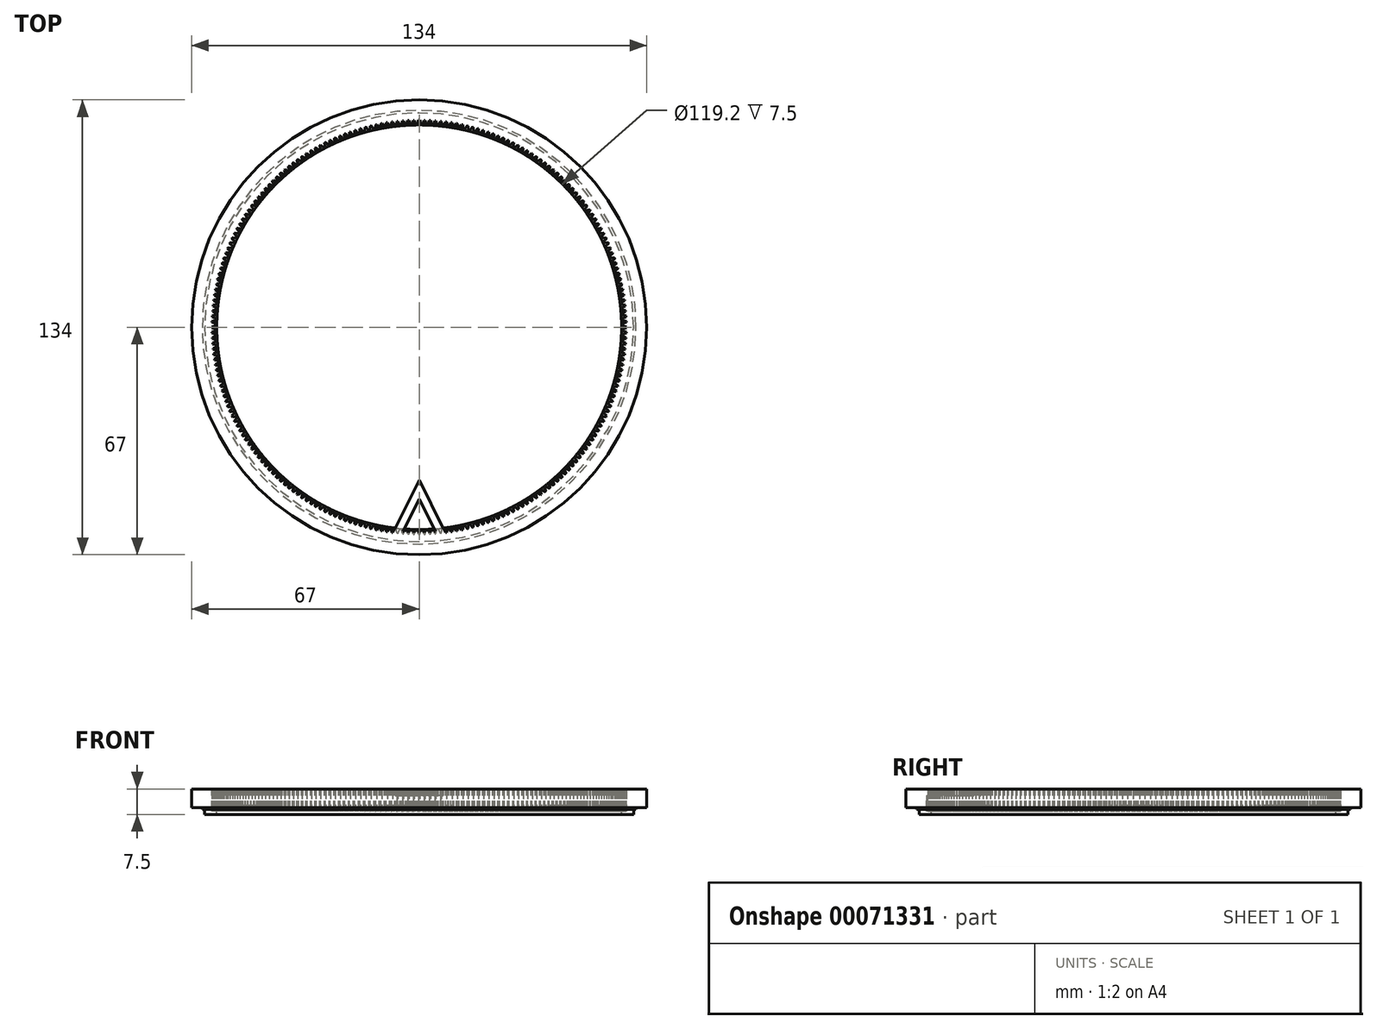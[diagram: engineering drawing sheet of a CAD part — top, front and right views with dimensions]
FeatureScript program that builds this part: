
annotation { "Feature Type Name" : "Feature", "Feature Type Description" : "" }
export const myFeature = defineFeature(function(context is Context, id is Id, definition is map)
    precondition{}
    {
        {
            var Q0;
            Q0=qCreatedBy(makeId("Front.planeOp"),FACE);
            var sketch = newSketch(context, id + "F0", { "sketchPlane" : qUnion([Q0])});
            skCircle(sketch, "E0", {"center": v(0, 0) * mm, "radius": 67 * mm});
            skCircle(sketch, "E1", {"center": v(0, 0) * mm, "radius": 59.6 * mm});
            skSolve(sketch);
        }
        {
            var Q0;
            Q0=makeQuery(id+"F0.imprint","IMPRINT",FACE,{"disambiguationData":[TD([[makeQuery(id+"F0.imprint","IMPRINT",EDGE,{"derivedFrom":sQuery(id+"F0.wireOp",EDGE,"E0")}),1.0]])]});
            extrude(context, id + "F1", {"entities" : qUnion([Q0]), "depth" : 7.5 * mm});
        }
        {
            var Q0;
            Q0=makeQuery(id+"F1.opExtrude","CAP_FACE",FACE,{"disambiguationData":[OSD([sQuery(id+"F0.wireOp",EDGE,"E0"),sQuery(id+"F0.wireOp",EDGE,"E1")])],"isStart":false});
            var sketch = newSketch(context, id + "F2", { "sketchPlane" : qUnion([Q0])});
            skCircle(sketch, "E2", {"center": v(0, 0) * mm, "radius": 63.88 * mm});
            skCircle(sketch, "E3", {"center": v(0, 0) * mm, "radius": 63.12 * mm});
            skSolve(sketch);
        }
        {
            var Q0;
            Q0=makeQuery(id+"F2.imprint","IMPRINT",FACE,{"disambiguationData":[TD([[makeQuery(id+"F2.imprint","IMPRINT",EDGE,{"derivedFrom":sQuery(id+"F2.wireOp",EDGE,"E2")}),1.0]])]});
            extrude(context, id + "F3", {"entities" : qUnion([Q0]), "operationType" : NewBodyOperationType.REMOVE, "oppositeDirection" : true, "depth" : 1.5 * mm});
        }
        {
            var Q0;
            {var subQ0=sQuery(id+"F0.wireOp",EDGE,"E0");Q0=makeQuery(id+"F3.boolean.opBoolean","SPLIT",FACE,{"disambiguationData":[TD([makeQuery(id+"F1.opExtrude","SWEPT_FACE",FACE,{"disambiguationData":[OSD([subQ0])]})])],"derivedFrom":makeQuery(id+"F1.opExtrude","CAP_FACE",FACE,{"disambiguationData":[OSD([subQ0,sQuery(id+"F0.wireOp",EDGE,"E1")])],"isStart":false})});}
            extrude(context, id + "F4", {"entities" : qUnion([Q0]), "operationType" : NewBodyOperationType.REMOVE, "oppositeDirection" : true, "depth" : 2 * mm});
        }
        {
            var Q0;
            Q0=makeQuery(id+"F1.opExtrude","CAP_FACE",FACE,{"disambiguationData":[OSD([sQuery(id+"F0.wireOp",EDGE,"E0"),sQuery(id+"F0.wireOp",EDGE,"E1")])],"isStart":true});
            var sketch = newSketch(context, id + "F5", { "sketchPlane" : qUnion([Q0])});
            skCircle(sketch, "E4", {"center": v(0, 0) * mm, "radius": 61 * mm});
            skLineSegment(sketch, "E5", {"start": v(0, 0) * mm, "end": v(61, 0) * mm});
            skLineSegment(sketch, "E6", {"start": v(61, 0.15) * mm, "end": v(61, -0.15) * mm});
            skPoint(sketch, "E7", {"position": v(59.4, 0) * mm});
            skLineSegment(sketch, "E8", {"start": v(59.4, 0.68) * mm, "end": v(59.4, -0.68) * mm});
            skLineSegment(sketch, "E9", {"start": v(59.4, 0.67) * mm, "end": v(61, 0.15) * mm});
            skLineSegment(sketch, "E10", {"start": v(59.4, -0.67) * mm, "end": v(61, -0.15) * mm});
            skSolve(sketch);
        }
        {
            var Q0;
            {var subQ1=sQuery(id+"F5.wireOp",EDGE,"E4");var subQ3=sQuery(id+"F5.wireOp",EDGE,"E9");var subQ4=makeQuery(id+"F5.imprint","INTERSECT",VERTEX,{"derivedFrom":[subQ1,subQ3]});Q0=makeQuery(id+"F5.imprint","IMPRINT",FACE,{"disambiguationData":[TD([[makeQuery(id+"F5.imprint","IMPRINT",EDGE,{"disambiguationData":[TD([[subQ4,1.0]])],"derivedFrom":subQ3}),-1.0]])]});}
            var Q1;
            {var subQ1=sQuery(id+"F5.wireOp",EDGE,"E4");var subQ3=sQuery(id+"F5.wireOp",EDGE,"E10");var subQ4=makeQuery(id+"F5.imprint","INTERSECT",VERTEX,{"derivedFrom":[subQ1,subQ3]});Q1=makeQuery(id+"F5.imprint","IMPRINT",FACE,{"disambiguationData":[TD([[makeQuery(id+"F5.imprint","IMPRINT",EDGE,{"disambiguationData":[TD([[subQ4,1.0]])],"derivedFrom":subQ3}),1.0]])]});}
            extrude(context, id + "F6", {"entities" : qUnion([Q0, Q1]), "operationType" : NewBodyOperationType.REMOVE, "oppositeDirection" : true, "depth" : 6.5 * mm});
        }
        {
            var Q0;
            Q0=makeQuery(id+"F6.boolean.opBoolean","COPY",FACE,{"derivedFrom":makeQuery(id+"F6.opExtrude","SWEPT_FACE",FACE,{"disambiguationData":[OSD([sQuery(id+"F5.wireOp",EDGE,"E4")])]})});
            var Q1;
            Q1=makeQuery(id+"F6.boolean.opBoolean","COPY",FACE,{"derivedFrom":makeQuery(id+"F6.opExtrude","SWEPT_FACE",FACE,{"disambiguationData":[OSD([sQuery(id+"F5.wireOp",EDGE,"E9")])]})});
            var Q2;
            Q2=makeQuery(id+"F6.boolean.opBoolean","COPY",FACE,{"derivedFrom":makeQuery(id+"F6.opExtrude","SWEPT_FACE",FACE,{"disambiguationData":[OSD([sQuery(id+"F5.wireOp",EDGE,"E10")])]})});
            var Q3;
            Q3=makeQuery(id+"F6.boolean.opBoolean","COPY",FACE,{"derivedFrom":makeQuery(id+"F6.opExtrude","CAP_FACE",FACE,{"disambiguationData":[OSD([sQuery(id+"F0.wireOp",EDGE,"E1"),sQuery(id+"F5.wireOp",EDGE,"E4"),sQuery(id+"F5.wireOp",EDGE,"E9"),sQuery(id+"F5.wireOp",EDGE,"E10")])],"isStart":false})});
            var Q4;
            Q4=sQuery(id+"F5.wireOp",EDGE,"E4");
            circularPattern(context, id + "F7", {"faces" : qUnion([Q0, Q1, Q2, Q3]), "axis" : qUnion([Q4]), "angle" : 360 * degree, "instanceCount" : 240, "equalSpace" : true, "patternType" : PatternType.FACE});
        }
        {
            var Q0;
            Q0=makeQuery(id+"F5.imprint","IMPRINT",FACE,{"disambiguationData":[TD([[makeQuery(id+"F5.imprint","IMPRINT",EDGE,{"derivedFrom":makeQuery(id+"F1.opExtrude","CAP_EDGE",EDGE,{"disambiguationData":[OSD([sQuery(id+"F0.wireOp",EDGE,"E0")])],"isStart":true})}),-1.0]])]});
            var sketch = newSketch(context, id + "F8", { "sketchPlane" : qUnion([Q0])});
            skLineSegment(sketch, "E11", {"start": v(0, 62.58) * mm, "end": v(8.8, 62.58) * mm});
            skLineSegment(sketch, "E12", {"start": v(8.8, 62.58) * mm, "end": v(0, 45) * mm});
            skLineSegment(sketch, "E13.MirrorCS", {"start": v(0, 62.58) * mm, "end": v(-8.8, 62.58) * mm});
            skLineSegment(sketch, "E14.MirrorCS", {"start": v(-8.8, 62.58) * mm, "end": v(0, 45) * mm});
            skLineSegment(sketch, "E15.0", {"start": v(0, 60.08) * mm, "end": v(4.75, 60.08) * mm});
            skLineSegment(sketch, "E15.1", {"start": v(0, 60.08) * mm, "end": v(-4.75, 60.08) * mm});
            skLineSegment(sketch, "E15.2", {"start": v(-4.75, 60.08) * mm, "end": v(0, 50.59) * mm});
            skLineSegment(sketch, "E15.3", {"start": v(4.75, 60.08) * mm, "end": v(0, 50.59) * mm});
            skSolve(sketch);
        }
        {
            var Q0;
            Q0 = qSketchRegion(id + "F8", true);
            extrude(context, id + "F9", {"entities" : qUnion([Q0]), "operationType" : NewBodyOperationType.ADD, "oppositeDirection" : true, "depth" : 2 * mm});
        }
        {
            var Q0;
            {var subQ1=sQuery(id+"F5.wireOp",EDGE,"E8");var subQ5=sQuery(id+"F5.wireOp",EDGE,"E9");var subQ6=makeQuery(id+"F5.imprint","INTERSECT",VERTEX,{"derivedFrom":[subQ1,subQ5]});Q0=makeQuery(id+"F5.imprint","IMPRINT",FACE,{"disambiguationData":[TD([[makeQuery(id+"F5.imprint","IMPRINT",EDGE,{"disambiguationData":[TD([[subQ6,-1.0]])],"derivedFrom":subQ1}),-1.0]])]});}
            var sketch = newSketch(context, id + "F10", { "sketchPlane" : qUnion([Q0])});
            skLineSegment(sketch, "E16", {"start": v(0, 0) * mm, "end": v(-77.68, 0) * mm});
            skSolve(sketch);
        }
        {
            var Q0;
            Q0=makeQuery(id+"F1.opExtrude","SWEPT_BODY",BODY,{"disambiguationData":[OSD([sQuery(id+"F0.wireOp",EDGE,"E0"),sQuery(id+"F0.wireOp",EDGE,"E1")])]});
            var Q1;
            Q1=sQuery(id+"F10.wireOp",EDGE,"E16");
            transform(context, id + "F11", {"entities" : qUnion([Q0]), "transformType" : TransformType.ROTATION, "transformAxis" : qUnion([Q1]), "angle" : 90 * degree, "makeCopy" : false});
        }
    });
